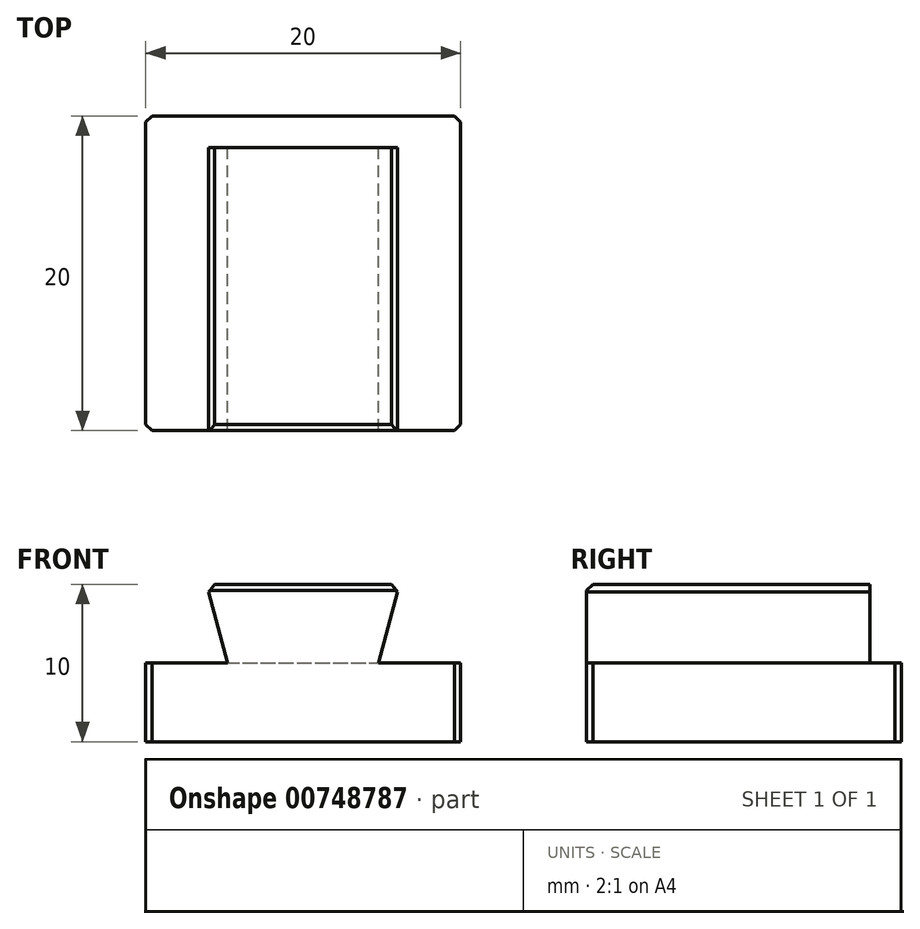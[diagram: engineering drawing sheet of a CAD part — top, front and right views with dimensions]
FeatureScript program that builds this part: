
annotation { "Feature Type Name" : "Feature", "Feature Type Description" : "" }
export const myFeature = defineFeature(function(context is Context, id is Id, definition is map)
    precondition{}
    {
        {
            assignVariable(context, id + "F0", {"name" : "PrintOffset", "anyValue" : 0.4});
        }
        {
            assignVariable(context, id + "F1", {"name" : "DovetailBackstopDepth", "anyValue" : 2});
        }
        {
            assignVariable(context, id + "F2", {"name" : "DovetailDepth", "anyValue" : 20});
        }
        {
            var Q0;
            Q0=qCreatedBy(makeId("Front.planeOp"),FACE);
            var sketch = newSketch(context, id + "F3", { "sketchPlane" : qUnion([Q0])});
            skLineSegment(sketch, "E0", {"start": v(-10, 0) * mm, "end": v(10, 0) * mm});
            skLineSegment(sketch, "E1", {"start": v(-10, 0) * mm, "end": v(-10, 10) * mm});
            skLineSegment(sketch, "E2", {"start": v(10, 10) * mm, "end": v(10, 0) * mm});
            skLineSegment(sketch, "E3", {"start": v(-10, 5) * mm, "end": v(10, 5) * mm});
            skLineSegment(sketch, "E4", {"start": v(-10, 10) * mm, "end": v(10, 10) * mm});
            skLineSegment(sketch, "E5", {"start": v(-6.14, 10) * mm, "end": v(-4.8, 5) * mm});
            skLineSegment(sketch, "E6", {"start": v(0, 0) * mm, "end": v(0, 10) * mm, "construction": true});
            skLineSegment(sketch, "E7.MirrorCS", {"start": v(6.14, 10) * mm, "end": v(4.8, 5) * mm});
            skSolve(sketch);
        }
        {
            var Q0;
            Q0=makeQuery(id+"F3.imprint","IMPRINT",FACE,{"disambiguationData":[TD([[makeQuery(id+"F3.imprint","IMPRINT",EDGE,{"derivedFrom":sQuery(id+"F3.wireOp",EDGE,"E0")}),1.0]])]});
            var Q1;
            {var subQ0=sQuery(id+"F3.wireOp",EDGE,"E5");Q1=makeQuery(id+"F3.imprint","IMPRINT",FACE,{"disambiguationData":[TD([[makeQuery(id+"F3.imprint","IMPRINT",EDGE,{"derivedFrom":subQ0}),1.0]])]});}
            extrude(context, id + "F4", {"entities" : qUnion([Q0, Q1]), "flatOperationType" : FlatOperationType.REMOVE, "offsetDistance" : 25 * mm, "depth" : (getVariable(context, 'DovetailDepth')) * mm, "domain" : OperationDomain.MODEL});
        }
        {
            var Q0;
            {var subQ0=sQuery(id+"F3.wireOp",EDGE,"E5");Q0=makeQuery(id+"F3.imprint","IMPRINT",FACE,{"disambiguationData":[TD([[makeQuery(id+"F3.imprint","IMPRINT",EDGE,{"derivedFrom":subQ0}),1.0]])]});}
            extrude(context, id + "F5", {"entities" : qUnion([Q0]), "operationType" : NewBodyOperationType.REMOVE, "depth" : (getVariable(context, 'DovetailBackstopDepth')) * mm});
        }
        {
            var Q0;
            Q0=makeQuery(id+"F4.opExtrude","SWEPT_EDGE",EDGE,{"disambiguationData":[OSD([sQuery(id+"F3.wireOp",EDGE,"E4"),sQuery(id+"F3.wireOp",EDGE,"E7.MirrorCS")])]});
            var Q1;
            Q1=makeQuery(id+"F4.opExtrude","SWEPT_EDGE",EDGE,{"disambiguationData":[OSD([sQuery(id+"F3.wireOp",EDGE,"E4"),sQuery(id+"F3.wireOp",EDGE,"E5")])]});
            var Q2;
            Q2=makeQuery(id+"F4.opExtrude","CAP_EDGE",EDGE,{"disambiguationData":[OSD([sQuery(id+"F3.wireOp",EDGE,"E4")])],"isStart":false});
            var Q3;
            Q3=makeQuery(id+"F5.boolean.opBoolean","COPY",EDGE,{"derivedFrom":makeQuery(id+"F5.opExtrude","CAP_EDGE",EDGE,{"disambiguationData":[OSD([sQuery(id+"F3.wireOp",EDGE,"E4")])],"isStart":false})});
            var Q4;
            Q4=makeQuery(id+"F4.opExtrude","CAP_EDGE",EDGE,{"disambiguationData":[OSD([sQuery(id+"F3.wireOp",EDGE,"E2")])],"isStart":false});
            var Q5;
            Q5=makeQuery(id+"F4.opExtrude","CAP_EDGE",EDGE,{"disambiguationData":[OSD([sQuery(id+"F3.wireOp",EDGE,"E2")])],"isStart":true});
            var Q6;
            Q6=makeQuery(id+"F4.opExtrude","CAP_EDGE",EDGE,{"disambiguationData":[OSD([sQuery(id+"F3.wireOp",EDGE,"E1")])],"isStart":false});
            var Q7;
            Q7=makeQuery(id+"F4.opExtrude","CAP_EDGE",EDGE,{"disambiguationData":[OSD([sQuery(id+"F3.wireOp",EDGE,"E1")])],"isStart":true});
            chamfer(context, id + "F6", {"entities" : qUnion([Q0, Q1, Q2, Q3, Q4, Q5, Q6, Q7]), "width" : (getVariable(context, 'PrintOffset')) * mm, "tangentPropagation" : true});
        }
    });
